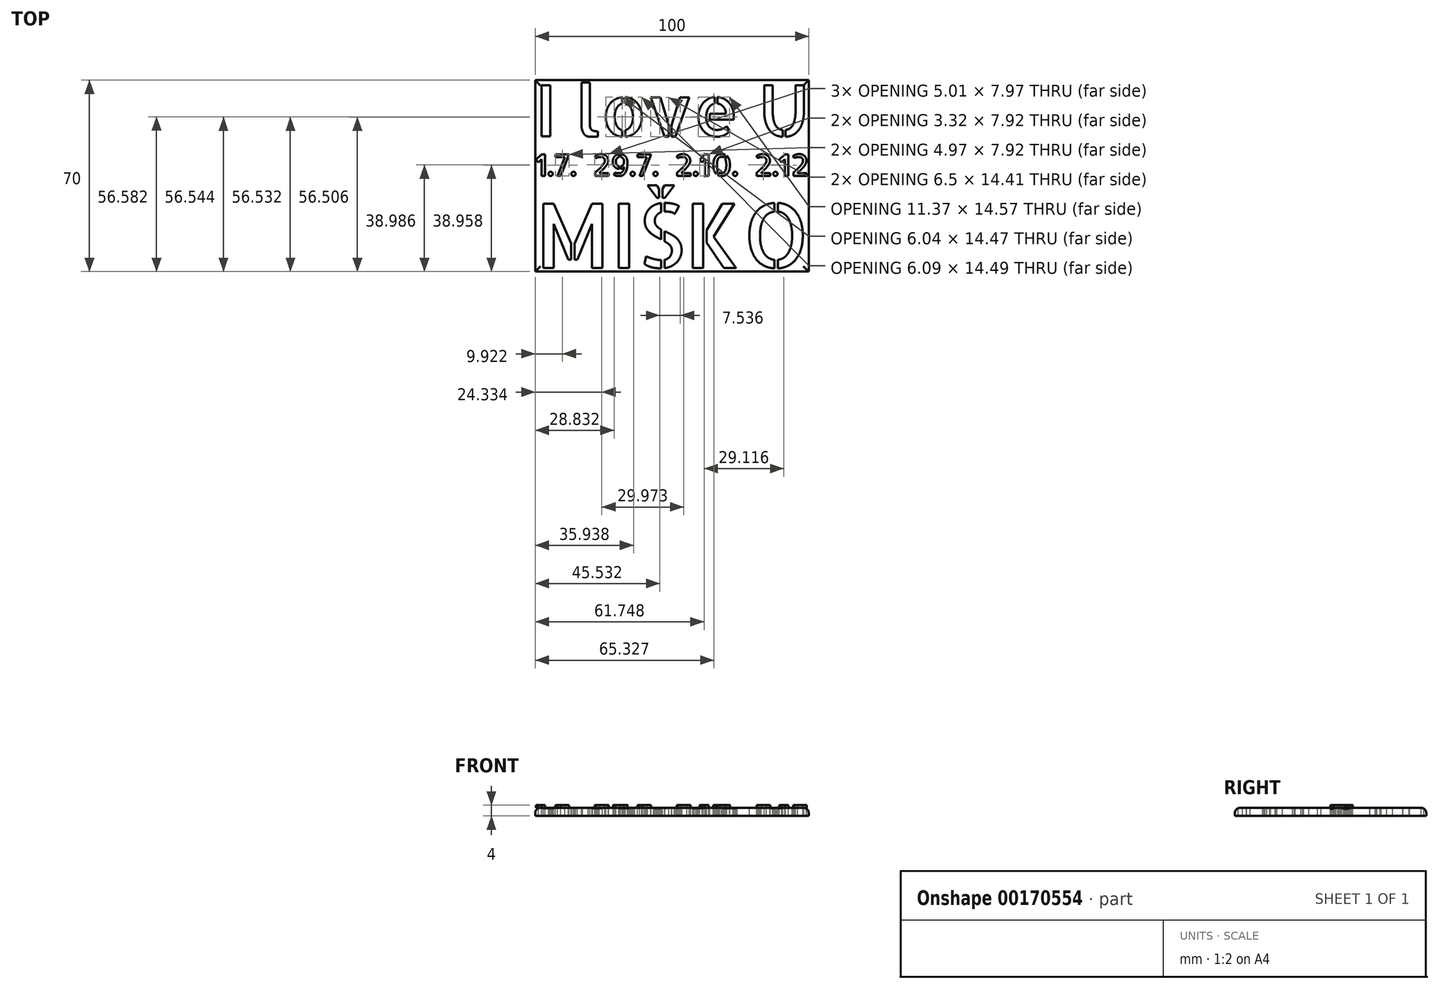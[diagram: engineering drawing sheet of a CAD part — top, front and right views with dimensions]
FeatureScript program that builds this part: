
annotation { "Feature Type Name" : "Feature", "Feature Type Description" : "" }
export const myFeature = defineFeature(function(context is Context, id is Id, definition is map)
    precondition{}
    {
        {
            var Q0;
            Q0=qCreatedBy(makeId("Top.planeOp"),FACE);
            var sketch = newSketch(context, id + "F0", { "sketchPlane" : qUnion([Q0])});
            skPoint(sketch, "E0.middle", {"position": v(0, 0) * mm});
            skLineSegment(sketch, "E1.bottom", {"start": v(50, -35) * mm, "end": v(-50, -35) * mm});
            skLineSegment(sketch, "E1.top", {"start": v(50, 35) * mm, "end": v(-50, 35) * mm});
            skLineSegment(sketch, "E1.left", {"start": v(50, -35) * mm, "end": v(50, 35) * mm});
            skLineSegment(sketch, "E1.right", {"start": v(-50, -35) * mm, "end": v(-50, 35) * mm});
            skText(sketch, "E2", { "text": "I love U", "fontName": "AllertaStencil-Regular.ttf"});
            skText(sketch, "E3", { "text": "MIŠKO", "fontName": "AllertaStencil-Regular.ttf"});
            skText(sketch, "E4", { "text": "1.7.  29.7.  2.10.  2.12", "fontName": "AllertaStencil-Regular.ttf"});
            const initialGuessF0  = {"E2": [-0.05, 0.0144, 1, 0, 0.01871], "E3": [-0.05, -0.03368, 1, 0, 0.02346], "E4": [-0.05, 0, 1, 0, 0.00792]};
            skSetInitialGuess(sketch, initialGuessF0);
            skSolve(sketch);
        }
        {
            var Q0;
            Q0=makeQuery(id+"F0.imprint","IMPRINT",FACE,{"disambiguationData":[TD([[makeQuery(id+"F0.imprint","IMPRINT",EDGE,{"derivedFrom":sQuery(id+"F0.wireOp",EDGE,"E1.bottom")}),-1.0]])]});
            extrude(context, id + "F1", {"entities" : qUnion([Q0]), "oppositeDirection" : true, "depth" : 3 * mm});
        }
        {
            var Q0;
            Q0=makeQuery(id+"F1.opExtrude","CAP_EDGE",EDGE,{"disambiguationData":[OSD([sQuery(id+"F0.wireOp",EDGE,"E1.left")])],"isStart":true});
            var Q1;
            Q1=makeQuery(id+"F1.opExtrude","CAP_EDGE",EDGE,{"disambiguationData":[OSD([sQuery(id+"F0.wireOp",EDGE,"E1.top")])],"isStart":true});
            var Q2;
            Q2=makeQuery(id+"F1.opExtrude","CAP_EDGE",EDGE,{"disambiguationData":[OSD([sQuery(id+"F0.wireOp",EDGE,"E1.right")])],"isStart":true});
            var Q3;
            Q3=makeQuery(id+"F1.opExtrude","CAP_EDGE",EDGE,{"disambiguationData":[OSD([sQuery(id+"F0.wireOp",EDGE,"E1.bottom")])],"isStart":true});
            fillet(context, id + "F2", {"entities" : qUnion([Q0, Q1, Q2, Q3]), "radius" : 2 * mm, "tangentPropagation" : true, "allowEdgeOverflow" : false});
        }
        {
            var Q0;
            Q0=makeQuery(id+"F0.imprint","IMPRINT",FACE,{"disambiguationData":[TD([[makeQuery(id+"F0.imprint","IMPRINT",EDGE,{"derivedFrom":sQuery(id+"F0.wireOp",EDGE,"E4.sketch_text.stroke-170")}),-1.0]])]});
            var Q1;
            Q1=makeQuery(id+"F0.imprint","IMPRINT",FACE,{"disambiguationData":[TD([[makeQuery(id+"F0.imprint","IMPRINT",EDGE,{"derivedFrom":sQuery(id+"F0.wireOp",EDGE,"E4.sketch_text.stroke-0")}),-1.0]])]});
            var Q2;
            Q2=makeQuery(id+"F0.imprint","IMPRINT",FACE,{"disambiguationData":[TD([[makeQuery(id+"F0.imprint","IMPRINT",EDGE,{"derivedFrom":sQuery(id+"F0.wireOp",EDGE,"E4.sketch_text.stroke-15")}),-1.0]])]});
            var Q3;
            Q3=makeQuery(id+"F0.imprint","IMPRINT",FACE,{"disambiguationData":[TD([[makeQuery(id+"F0.imprint","IMPRINT",EDGE,{"derivedFrom":sQuery(id+"F0.wireOp",EDGE,"E4.sketch_text.stroke-29")}),-1.0]])]});
            var Q4;
            Q4=makeQuery(id+"F0.imprint","IMPRINT",FACE,{"disambiguationData":[TD([[makeQuery(id+"F0.imprint","IMPRINT",EDGE,{"derivedFrom":sQuery(id+"F0.wireOp",EDGE,"E4.sketch_text.stroke-62")}),-1.0]])]});
            var Q5;
            Q5=makeQuery(id+"F0.imprint","IMPRINT",FACE,{"disambiguationData":[TD([[makeQuery(id+"F0.imprint","IMPRINT",EDGE,{"derivedFrom":sQuery(id+"F0.wireOp",EDGE,"E4.sketch_text.stroke-76")}),-1.0]])]});
            var Q6;
            Q6=makeQuery(id+"F0.imprint","IMPRINT",FACE,{"disambiguationData":[TD([[makeQuery(id+"F0.imprint","IMPRINT",EDGE,{"derivedFrom":sQuery(id+"F0.wireOp",EDGE,"E4.sketch_text.stroke-129")}),-1.0]])]});
            var Q7;
            Q7=makeQuery(id+"F0.imprint","IMPRINT",FACE,{"disambiguationData":[TD([[makeQuery(id+"F0.imprint","IMPRINT",EDGE,{"derivedFrom":sQuery(id+"F0.wireOp",EDGE,"E4.sketch_text.stroke-193")}),-1.0]])]});
            var Q8;
            Q8=makeQuery(id+"F0.imprint","IMPRINT",FACE,{"disambiguationData":[TD([[makeQuery(id+"F0.imprint","IMPRINT",EDGE,{"derivedFrom":sQuery(id+"F0.wireOp",EDGE,"E4.sketch_text.stroke-177")}),-1.0]])]});
            var Q9;
            Q9=makeQuery(id+"F0.imprint","IMPRINT",FACE,{"disambiguationData":[TD([[makeQuery(id+"F0.imprint","IMPRINT",EDGE,{"derivedFrom":sQuery(id+"F0.wireOp",EDGE,"E4.sketch_text.stroke-115")}),-1.0]])]});
            var Q10;
            Q10=makeQuery(id+"F0.imprint","IMPRINT",FACE,{"disambiguationData":[TD([[makeQuery(id+"F0.imprint","IMPRINT",EDGE,{"derivedFrom":sQuery(id+"F0.wireOp",EDGE,"E4.sketch_text.stroke-218")}),-1.0]])]});
            var Q11;
            Q11=makeQuery(id+"F0.imprint","IMPRINT",FACE,{"disambiguationData":[TD([[makeQuery(id+"F0.imprint","IMPRINT",EDGE,{"derivedFrom":sQuery(id+"F0.wireOp",EDGE,"E4.sketch_text.stroke-259")}),-1.0]])]});
            var Q12;
            Q12=makeQuery(id+"F0.imprint","IMPRINT",FACE,{"disambiguationData":[TD([[makeQuery(id+"F0.imprint","IMPRINT",EDGE,{"derivedFrom":sQuery(id+"F0.wireOp",EDGE,"E4.sketch_text.stroke-266")}),-1.0]])]});
            extrude(context, id + "F3", {"entities" : qUnion([Q0, Q1, Q2, Q3, Q4, Q5, Q6, Q7, Q8, Q9, Q10, Q11, Q12]), "depth" : 1 * mm});
        }
    });
